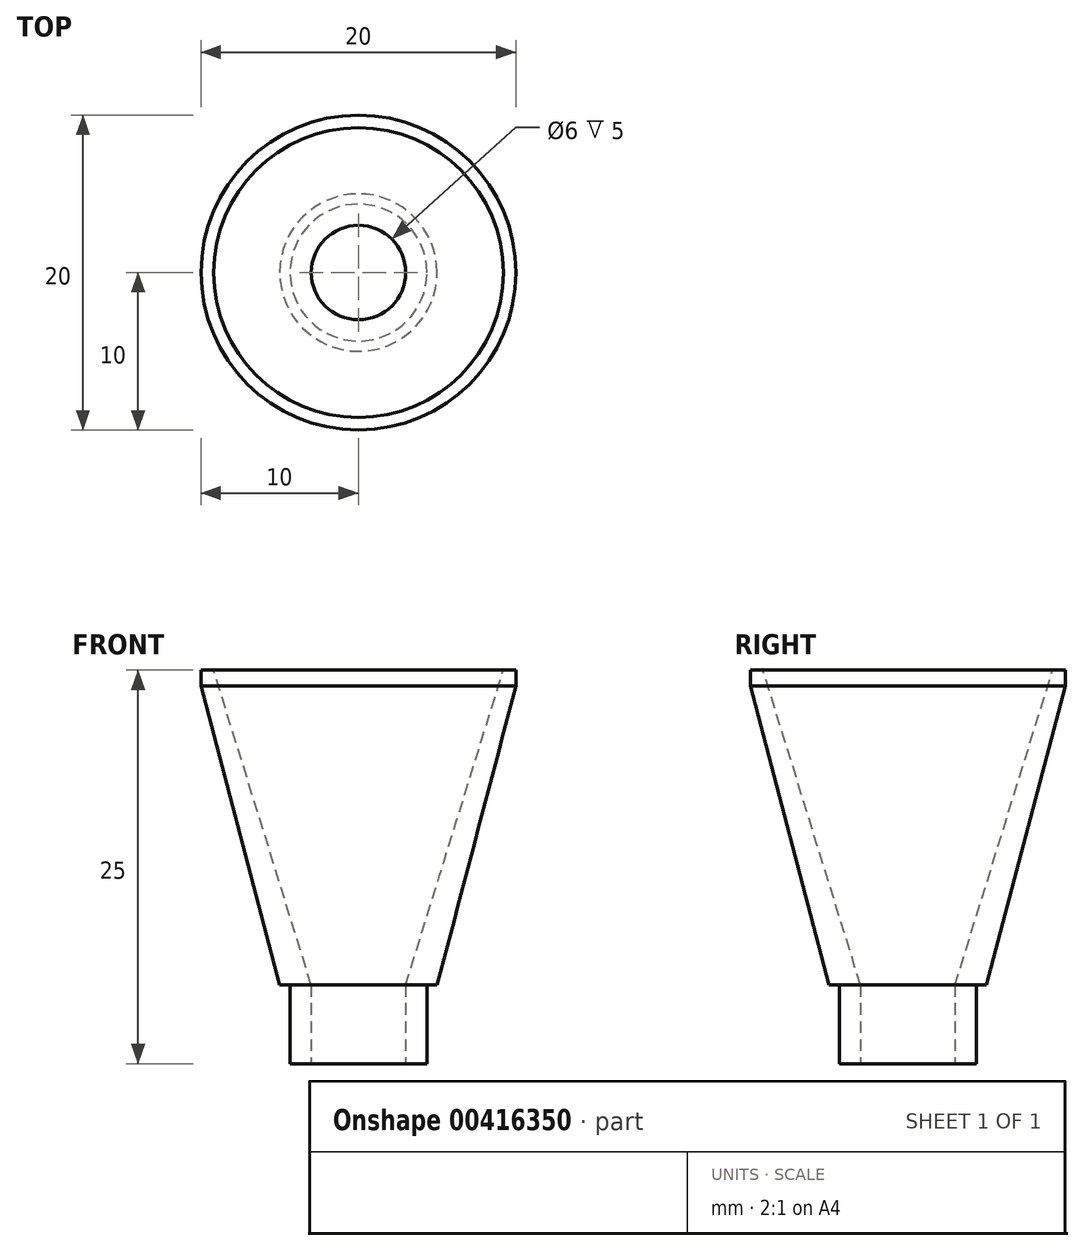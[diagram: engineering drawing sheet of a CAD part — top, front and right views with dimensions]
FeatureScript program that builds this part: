
annotation { "Feature Type Name" : "Feature", "Feature Type Description" : "" }
export const myFeature = defineFeature(function(context is Context, id is Id, definition is map)
    precondition{}
    {
        {
            var Q0;
            Q0=qCreatedBy(makeId("Top.planeOp"),FACE);
            var sketch = newSketch(context, id + "F0", { "sketchPlane" : qUnion([Q0])});
            skCircle(sketch, "E0", {"center": v(0, 0) * mm, "radius": 3 * mm});
            skCircle(sketch, "E1", {"center": v(0, 0) * mm, "radius": 4.35 * mm});
            skSolve(sketch);
        }
        {
            var Q0;
            Q0 = qSketchRegion(id + "F0", true);
            extrude(context, id + "F1", {"entities" : qUnion([Q0]), "depth" : 5 * mm});
        }
        {
            var Q0;
            Q0=makeQuery(id+"F1.opExtrude","CAP_FACE",FACE,{"disambiguationData":[OSD([sQuery(id+"F0.wireOp",EDGE,"E0"),sQuery(id+"F0.wireOp",EDGE,"E1")])],"isStart":false});
            var sketch = newSketch(context, id + "F2", { "sketchPlane" : qUnion([Q0])});
            skPoint(sketch, "E2.0", {"position": v(0, 0) * mm});
            skCircle(sketch, "E3", {"center": v(0, 0) * mm, "radius": 3 * mm});
            skCircle(sketch, "E4", {"center": v(0, 0) * mm, "radius": 10 * mm});
            skSolve(sketch);
        }
        {
            var Q0;
            Q0 = qSketchRegion(id + "F2", true);
            extrude(context, id + "F3", {"entities" : qUnion([Q0]), "operationType" : NewBodyOperationType.ADD, "depth" : 20 * mm});
        }
        {
            var Q0;
            Q0=makeQuery(id+"F3.opExtrude","CAP_EDGE",EDGE,{"disambiguationData":[OSD([sQuery(id+"F2.wireOp",EDGE,"E3")])],"isStart":false});
            chamfer(context, id + "F4", {"entities" : qUnion([Q0]), "chamferType" : ChamferType.TWO_OFFSETS, "width1" : 20 * mm, "oppositeDirection" : false, "width2" : 6.2 * mm, "tangentPropagation" : true});
        }
        {
            var Q0;
            Q0=makeQuery(id+"F3.opExtrude","CAP_EDGE",EDGE,{"disambiguationData":[OSD([sQuery(id+"F2.wireOp",EDGE,"E4")])],"isStart":true});
            chamfer(context, id + "F5", {"entities" : qUnion([Q0]), "chamferType" : ChamferType.TWO_OFFSETS, "width1" : 19 * mm, "oppositeDirection" : false, "width2" : 5 * mm, "tangentPropagation" : true});
        }
    });
